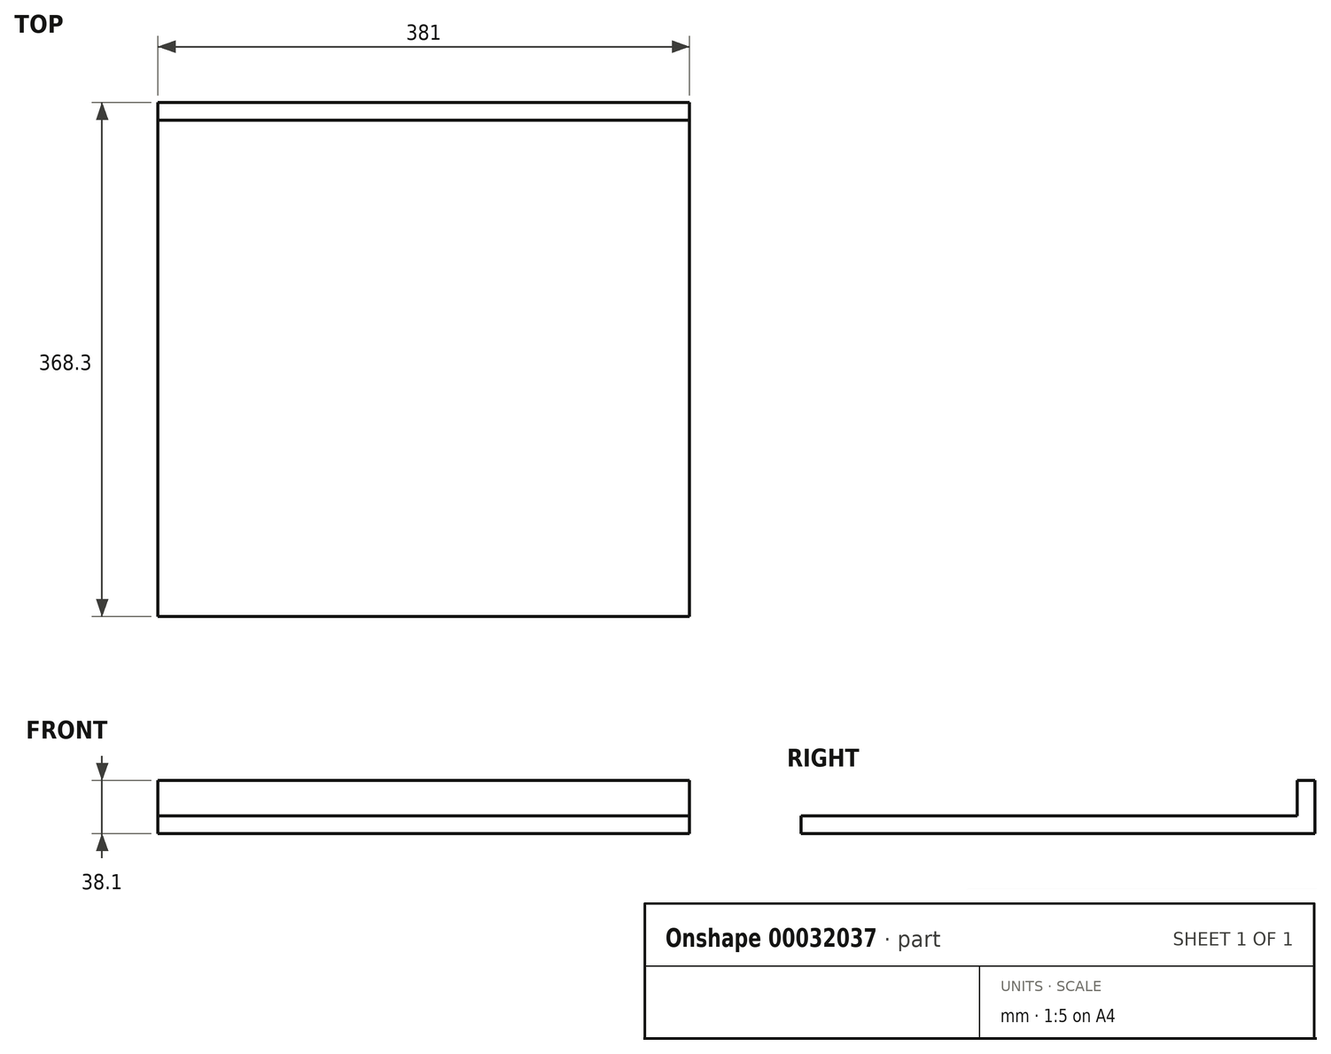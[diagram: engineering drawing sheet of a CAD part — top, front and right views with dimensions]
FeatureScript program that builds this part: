
annotation { "Feature Type Name" : "Feature", "Feature Type Description" : "" }
export const myFeature = defineFeature(function(context is Context, id is Id, definition is map)
    precondition{}
    {
        {
            var Q0;
            Q0=qCreatedBy(makeId("Top.planeOp"),FACE);
            var sketch = newSketch(context, id + "F0", { "sketchPlane" : qUnion([Q0])});
            skLineSegment(sketch, "E0.rect.bottom", {"start": v(190.5, 184.15) * mm, "end": v(-190.5, 184.15) * mm});
            skLineSegment(sketch, "E0.rect.top", {"start": v(190.5, -184.15) * mm, "end": v(-190.5, -184.15) * mm});
            skLineSegment(sketch, "E0.rect.left", {"start": v(190.5, 184.15) * mm, "end": v(190.5, -184.15) * mm});
            skLineSegment(sketch, "E0.rect.right", {"start": v(-190.5, 184.15) * mm, "end": v(-190.5, -184.15) * mm});
            skPoint(sketch, "E0.rect.middle", {"position": v(0, 0) * mm});
            skSolve(sketch);
        }
        {
            var Q0;
            Q0=makeQuery(id+"F0.imprint","IMPRINT",FACE,{"disambiguationData":[TD([[makeQuery(id+"F0.imprint","IMPRINT",EDGE,{"derivedFrom":sQuery(id+"F0.wireOp",EDGE,"E0.rect.bottom")}),1.0]])]});
            extrude(context, id + "F1", {"entities" : qUnion([Q0]), "depth" : 12.7 * mm});
        }
        {
            var Q0;
            Q0=makeQuery(id+"F1.opExtrude","CAP_FACE",FACE,{"disambiguationData":[OSD([sQuery(id+"F0.wireOp",EDGE,"E0.rect.bottom"),sQuery(id+"F0.wireOp",EDGE,"E0.rect.top"),sQuery(id+"F0.wireOp",EDGE,"E0.rect.left"),sQuery(id+"F0.wireOp",EDGE,"E0.rect.right")])],"isStart":false});
            var sketch = newSketch(context, id + "F2", { "sketchPlane" : qUnion([Q0])});
            skLineSegment(sketch, "E1", {"start": v(-190.5, 184.15) * mm, "end": v(-190.5, 171.45) * mm});
            skLineSegment(sketch, "E2.bottom", {"start": v(-190.5, 171.45) * mm, "end": v(190.5, 171.45) * mm});
            skLineSegment(sketch, "E2.top", {"start": v(-190.5, 184.15) * mm, "end": v(190.5, 184.15) * mm});
            skLineSegment(sketch, "E2.left", {"start": v(-190.5, 171.45) * mm, "end": v(-190.5, 184.15) * mm});
            skLineSegment(sketch, "E2.right", {"start": v(190.5, 171.45) * mm, "end": v(190.5, 184.15) * mm});
            skLineSegment(sketch, "E3", {"start": v(190.5, 171.45) * mm, "end": v(177.8, 171.45) * mm});
            skLineSegment(sketch, "E4.bottom", {"start": v(177.8, 171.45) * mm, "end": v(190.5, 171.45) * mm});
            skLineSegment(sketch, "E4.top", {"start": v(177.8, -184.15) * mm, "end": v(190.5, -184.15) * mm});
            skLineSegment(sketch, "E4.left", {"start": v(177.8, 171.45) * mm, "end": v(177.8, -184.15) * mm});
            skLineSegment(sketch, "E4.right", {"start": v(190.5, 171.45) * mm, "end": v(190.5, -184.15) * mm});
            skLineSegment(sketch, "E5", {"start": v(177.8, -184.15) * mm, "end": v(177.8, -171.45) * mm});
            skLineSegment(sketch, "E6.left", {"start": v(177.8, -171.45) * mm, "end": v(177.8, -184.15) * mm});
            skLineSegment(sketch, "E6.right", {"start": v(-190.5, -171.45) * mm, "end": v(-190.5, -184.15) * mm});
            skLineSegment(sketch, "E7", {"start": v(-190.5, 171.45) * mm, "end": v(-177.8, 171.45) * mm});
            skLineSegment(sketch, "E8.bottom", {"start": v(-177.8, 171.45) * mm, "end": v(-190.5, 171.45) * mm});
            skLineSegment(sketch, "E8.top", {"start": v(-177.8, -184.15) * mm, "end": v(-190.5, -184.15) * mm});
            skLineSegment(sketch, "E8.left", {"start": v(-177.8, 171.45) * mm, "end": v(-177.8, -184.15) * mm});
            skLineSegment(sketch, "E8.right", {"start": v(-190.5, 171.45) * mm, "end": v(-190.5, -184.15) * mm});
            skSolve(sketch);
        }
        {
            var Q0;
            {var subQ1=sQuery(id+"F2.wireOp",EDGE,"E8.bottom");Q0=makeQuery(id+"F2.imprint","IMPRINT",FACE,{"disambiguationData":[TD([[makeQuery(id+"F2.imprint","IMPRINT",EDGE,{"derivedFrom":subQ1}),1.0]])]});}
            var Q1;
            Q1=makeQuery(id+"F2.imprint","IMPRINT",FACE,{"disambiguationData":[TD([[makeQuery(id+"F2.imprint","IMPRINT",EDGE,{"derivedFrom":sQuery(id+"F2.wireOp",EDGE,"E2.bottom")}),1.0]])]});
            var Q2;
            Q2=makeQuery(id+"F2.imprint","IMPRINT",FACE,{"disambiguationData":[TD([[makeQuery(id+"F2.imprint","IMPRINT",EDGE,{"derivedFrom":sQuery(id+"F2.wireOp",EDGE,"E4.bottom")}),-1.0]])]});
            extrude(context, id + "F3", {"entities" : qUnion([Q0, Q1, Q2]), "operationType" : NewBodyOperationType.ADD, "depth" : 25.4 * mm});
        }
    });
